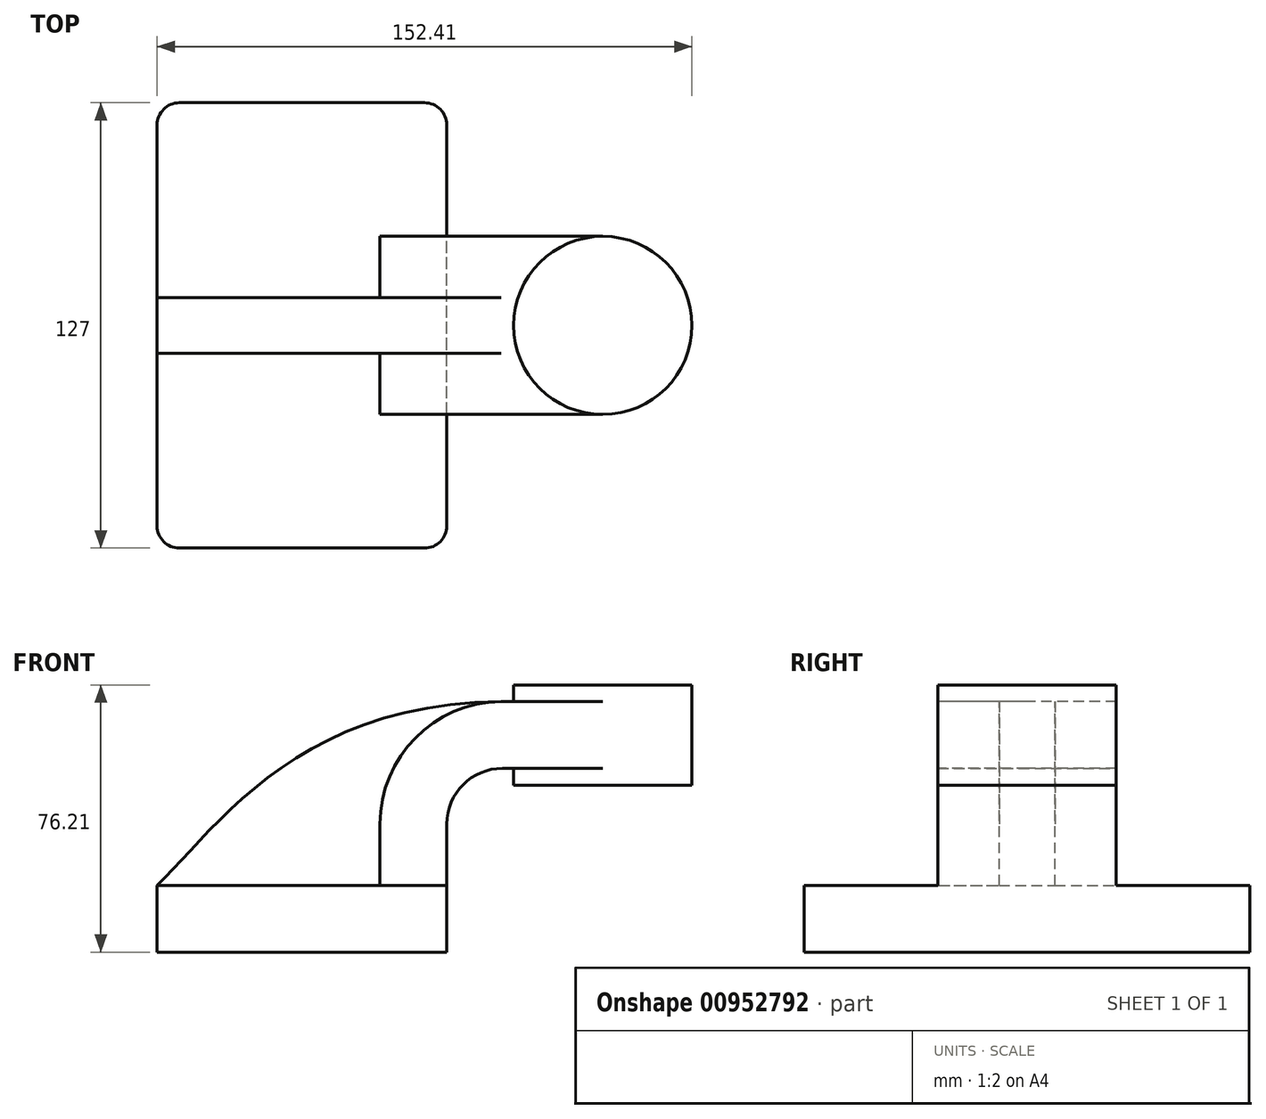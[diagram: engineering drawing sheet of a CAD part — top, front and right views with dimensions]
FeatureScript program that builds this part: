
annotation { "Feature Type Name" : "Feature", "Feature Type Description" : "" }
export const myFeature = defineFeature(function(context is Context, id is Id, definition is map)
    precondition{}
    {
        {
            var Q0;
            Q0=qCreatedBy(makeId("Front.planeOp"),FACE);
            var sketch = newSketch(context, id + "F0", { "sketchPlane" : qUnion([Q0])});
            skLineSegment(sketch, "E0.bottom", {"start": v(-41.28, 9.52) * mm, "end": v(41.27, 9.53) * mm});
            skLineSegment(sketch, "E0.top", {"start": v(-41.28, -9.53) * mm, "end": v(41.28, -9.53) * mm});
            skLineSegment(sketch, "E0.left", {"start": v(-41.28, 9.52) * mm, "end": v(-41.27, -9.53) * mm});
            skLineSegment(sketch, "E0.right", {"start": v(41.28, 9.53) * mm, "end": v(41.28, -9.52) * mm});
            skPoint(sketch, "E0.middle", {"position": v(0, 0) * mm});
            skLineSegment(sketch, "E1.bottom", {"start": v(111.12, 38.1) * mm, "end": v(60.32, 38.1) * mm});
            skLineSegment(sketch, "E1.top", {"start": v(111.12, 66.68) * mm, "end": v(60.32, 66.68) * mm});
            skLineSegment(sketch, "E1.left", {"start": v(111.12, 38.1) * mm, "end": v(111.12, 66.68) * mm});
            skLineSegment(sketch, "E1.right", {"start": v(60.32, 38.1) * mm, "end": v(60.32, 66.68) * mm});
            skPoint(sketch, "E1.middle", {"position": v(85.72, 52.39) * mm});
            skLineSegment(sketch, "E2", {"start": v(41.27, 9.53) * mm, "end": v(41.27, 27) * mm});
            skArc(sketch, "E3", {"start": v(41.27, 27) * mm, "mid": v(45.92, 38.23) * mm, "end": v(57.15, 42.88) * mm});
            skLineSegment(sketch, "E4.0", {"start": v(57.15, 61.93) * mm, "end": v(85.72, 61.93) * mm});
            skArc(sketch, "E4.1", {"start": v(22.22, 27) * mm, "mid": v(32.45, 51.7) * mm, "end": v(57.15, 61.93) * mm});
            skLineSegment(sketch, "E4.2", {"start": v(22.22, 9.53) * mm, "end": v(22.22, 27) * mm});
            skLineSegment(sketch, "E5", {"start": v(85.72, 38.1) * mm, "end": v(85.72, 66.68) * mm});
            skFitSpline(sketch, "E6", {"points": [v(-41.28, 9.52) * mm, v(57.15, 61.93) * mm], "startDerivative": vector(50.49, 48.35) * mm, "endDerivative": vector(176.43, 0.78) * mm});
            skLineSegment(sketch, "E7", {"start": v(57.15, 42.88) * mm, "end": v(85.72, 42.88) * mm});
            skSolve(sketch);
        }
        {
            var Q0;
            Q0=makeQuery(id+"F0.imprint","IMPRINT",FACE,{"disambiguationData":[TD([[makeQuery(id+"F0.imprint","IMPRINT",EDGE,{"derivedFrom":sQuery(id+"F0.wireOp",EDGE,"E0.top")}),1.0]])]});
            extrude(context, id + "F1", {"entities" : qUnion([Q0]), "endBound" : BoundingType.SYMMETRIC, "depth" : 127 * mm, "offsetDistance" : 25.4 * mm});
        }
        {
            var Q0;
            {var subQ1=sQuery(id+"F0.wireOp",EDGE,"E2");Q0=makeQuery(id+"F0.imprint","IMPRINT",FACE,{"disambiguationData":[TD([[makeQuery(id+"F0.imprint","IMPRINT",EDGE,{"derivedFrom":subQ1}),1.0]])]});}
            var Q1;
            {var subQ0=sQuery(id+"F0.wireOp",EDGE,"E7");var subQ1=sQuery(id+"F0.wireOp",EDGE,"E1.right");var subQ2=makeQuery(id+"F0.imprint","INTERSECT",VERTEX,{"derivedFrom":[subQ1,subQ0]});Q1=makeQuery(id+"F0.imprint","IMPRINT",FACE,{"disambiguationData":[TD([[makeQuery(id+"F0.imprint","IMPRINT",EDGE,{"disambiguationData":[TD([[subQ2,-1.0]])],"derivedFrom":subQ1}),-1.0]])]});}
            extrude(context, id + "F2", {"entities" : qUnion([Q0, Q1]), "operationType" : NewBodyOperationType.ADD, "endBound" : BoundingType.SYMMETRIC, "depth" : 50.8 * mm, "offsetDistance" : 25.4 * mm});
        }
        {
            var Q0;
            {var subQ3=sQuery(id+"F0.wireOp",EDGE,"E4.2");Q0=makeQuery(id+"F0.imprint","IMPRINT",FACE,{"disambiguationData":[TD([[makeQuery(id+"F0.imprint","IMPRINT",EDGE,{"derivedFrom":subQ3}),1.0]])]});}
            extrude(context, id + "F3", {"entities" : qUnion([Q0]), "operationType" : NewBodyOperationType.ADD, "endBound" : BoundingType.SYMMETRIC, "depth" : 15.88 * mm, "offsetDistance" : 25.4 * mm});
        }
        {
            var Q0;
            {var subQ4=sQuery(id+"F0.wireOp",EDGE,"E1.left");Q0=makeQuery(id+"F0.imprint","IMPRINT",FACE,{"disambiguationData":[TD([[makeQuery(id+"F0.imprint","IMPRINT",EDGE,{"derivedFrom":subQ4}),1.0]])]});}
            var Q1;
            Q1=sQuery(id+"F0.wireOp",EDGE,"E5");
            revolve(context, id + "F4", {"operationType" : NewBodyOperationType.ADD, "surfaceOperationType" : NewSurfaceOperationType.NEW, "entities" : qUnion([Q0]), "axis" : qUnion([Q1]), "revolveType" : RevolveType.FULL});
        }
        {
            var Q0;
            Q0=makeQuery(id+"F1.opExtrude","CAP_EDGE",EDGE,{"disambiguationData":[OSD([sQuery(id+"F0.wireOp",EDGE,"E0.left")])],"isStart":false});
            var Q1;
            Q1=makeQuery(id+"F1.opExtrude","CAP_EDGE",EDGE,{"disambiguationData":[OSD([sQuery(id+"F0.wireOp",EDGE,"E0.right")])],"isStart":false});
            var Q2;
            Q2=makeQuery(id+"F1.opExtrude","CAP_EDGE",EDGE,{"disambiguationData":[OSD([sQuery(id+"F0.wireOp",EDGE,"E0.right")])],"isStart":true});
            var Q3;
            Q3=makeQuery(id+"F1.opExtrude","CAP_EDGE",EDGE,{"disambiguationData":[OSD([sQuery(id+"F0.wireOp",EDGE,"E0.left")])],"isStart":true});
            fillet(context, id + "F5", {"entities" : qUnion([Q0, Q1, Q2, Q3]), "radius" : 6.35 * mm, "tangentPropagation" : true, "allowEdgeOverflow" : false});
        }
    });
